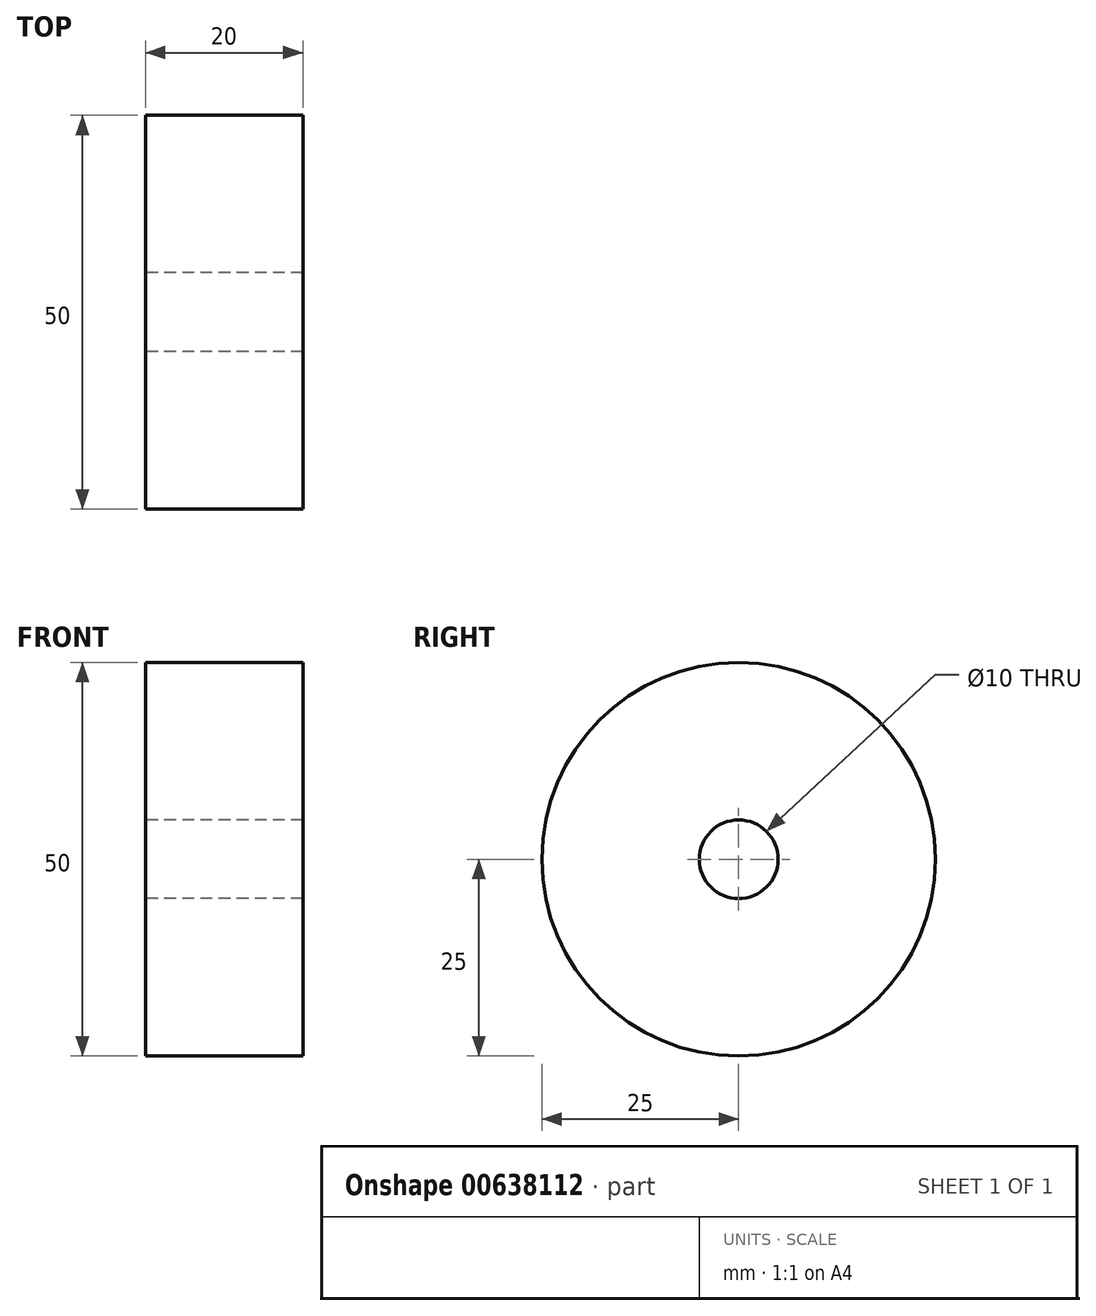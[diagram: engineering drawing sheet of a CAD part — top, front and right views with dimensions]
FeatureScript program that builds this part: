
annotation { "Feature Type Name" : "Feature", "Feature Type Description" : "" }
export const myFeature = defineFeature(function(context is Context, id is Id, definition is map)
    precondition{}
    {
        {
            var Q0;
            Q0=qCreatedBy(makeId("Right.planeOp"),FACE);
            var sketch = newSketch(context, id + "F0", { "sketchPlane" : qUnion([Q0])});
            skCircle(sketch, "E0", {"center": v(0, 0) * mm, "radius": 25 * mm});
            skCircle(sketch, "E1", {"center": v(0, 0) * mm, "radius": 5 * mm});
            skSolve(sketch);
        }
        {
            var Q0;
            Q0=makeQuery(id+"F0.imprint","IMPRINT",FACE,{"disambiguationData":[TD([[makeQuery(id+"F0.imprint","IMPRINT",EDGE,{"derivedFrom":sQuery(id+"F0.wireOp",EDGE,"E0")}),1.0]])]});
            extrude(context, id + "F1", {"entities" : qUnion([Q0]), "depth" : 20 * mm, "offsetDistance" : 25 * mm});
        }
    });
